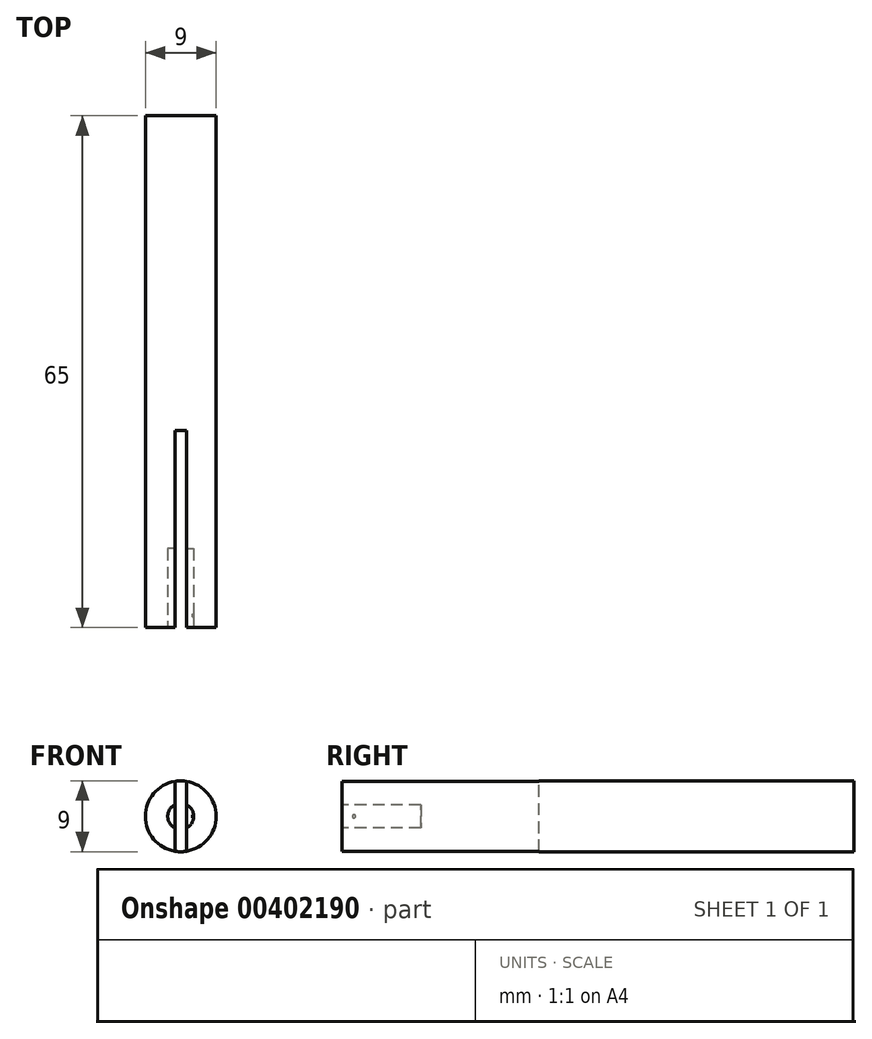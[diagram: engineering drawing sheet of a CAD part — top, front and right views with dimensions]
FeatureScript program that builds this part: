
annotation { "Feature Type Name" : "Feature", "Feature Type Description" : "" }
export const myFeature = defineFeature(function(context is Context, id is Id, definition is map)
    precondition{}
    {
        {
            var Q0;
            Q0=qCreatedBy(makeId("Front.planeOp"),FACE);
            var sketch = newSketch(context, id + "F0", { "sketchPlane" : qUnion([Q0])});
            skCircle(sketch, "E0", {"center": v(0, 0) * mm, "radius": 4.5 * mm});
            skSolve(sketch);
        }
        {
            var Q0;
            Q0=makeQuery(id+"F0.imprint","IMPRINT",FACE,{"disambiguationData":[TD([[makeQuery(id+"F0.imprint","IMPRINT",EDGE,{"derivedFrom":sQuery(id+"F0.wireOp",EDGE,"E0")}),1.0]])]});
            extrude(context, id + "F1", {"entities" : qUnion([Q0]), "oppositeDirection" : true, "depth" : 65 * mm});
        }
        {
            var Q0;
            Q0=makeQuery(id+"F1.opExtrude","CAP_FACE",FACE,{"disambiguationData":[OSD([sQuery(id+"F0.wireOp",EDGE,"E0")])],"isStart":true});
            var sketch = newSketch(context, id + "F2", { "sketchPlane" : qUnion([Q0])});
            skLineSegment(sketch, "E1.bottom", {"start": v(-0.75, -12.5) * mm, "end": v(0.75, -12.5) * mm});
            skLineSegment(sketch, "E1.top", {"start": v(-0.75, 12.5) * mm, "end": v(0.75, 12.5) * mm});
            skLineSegment(sketch, "E1.left", {"start": v(-0.75, -12.5) * mm, "end": v(-0.75, 12.5) * mm});
            skLineSegment(sketch, "E1.right", {"start": v(0.75, -12.5) * mm, "end": v(0.75, 12.5) * mm});
            skPoint(sketch, "E1.middle", {"position": v(0, 0) * mm});
            skSolve(sketch);
        }
        {
            var Q0;
            {var subQ0=sQuery(id+"F2.wireOp",EDGE,"E1.bottom");Q0=makeQuery(id+"F2.imprint","IMPRINT",FACE,{"disambiguationData":[TD([[makeQuery(id+"F2.imprint","IMPRINT",EDGE,{"derivedFrom":subQ0}),1.0]])]});}
            var Q1;
            {var subQ0=sQuery(id+"F2.wireOp",EDGE,"E1.left");var subQ1=makeQuery(id+"F1.opExtrude","CAP_EDGE",EDGE,{"disambiguationData":[OSD([sQuery(id+"F0.wireOp",EDGE,"E0")])],"isStart":true});var subQ2=makeQuery(id+"F2.imprint","INTERSECT",VERTEX,{"disambiguationData":[OD(0.0)],"derivedFrom":[subQ1,subQ0]});Q1=makeQuery(id+"F2.imprint","IMPRINT",FACE,{"disambiguationData":[TD([[makeQuery(id+"F2.imprint","IMPRINT",EDGE,{"disambiguationData":[TD([[subQ2,-1.0]])],"derivedFrom":subQ0}),-1.0]])]});}
            var Q2;
            {var subQ0=sQuery(id+"F2.wireOp",EDGE,"E1.top");Q2=makeQuery(id+"F2.imprint","IMPRINT",FACE,{"disambiguationData":[TD([[makeQuery(id+"F2.imprint","IMPRINT",EDGE,{"derivedFrom":subQ0}),-1.0]])]});}
            extrude(context, id + "F3", {"entities" : qUnion([Q0, Q1, Q2]), "operationType" : NewBodyOperationType.REMOVE, "oppositeDirection" : true, "depth" : 25 * mm});
        }
        {
            var Q0;
            {var subQ0=sQuery(id+"F0.wireOp",EDGE,"E0");Q0=makeQuery(id+"F3.boolean.opBoolean","SPLIT",FACE,{"disambiguationData":[TD([makeQuery(id+"F3.opExtrude","SWEPT_FACE",FACE,{"disambiguationData":[OSD([sQuery(id+"F2.wireOp",EDGE,"E1.right")])]})])],"derivedFrom":makeQuery(id+"F1.opExtrude","CAP_FACE",FACE,{"disambiguationData":[OSD([subQ0])],"isStart":true})});}
            var sketch = newSketch(context, id + "F4", { "sketchPlane" : qUnion([Q0])});
            skCircle(sketch, "E2", {"center": v(0, 0) * mm, "radius": 1.65 * mm});
            skSolve(sketch);
        }
        {
            var Q0;
            {var subQ0=sQuery(id+"F4.wireOp",EDGE,"E2");var subQ1=makeQuery(id+"F3.boolean.opBoolean","COPY",EDGE,{"derivedFrom":makeQuery(id+"F3.opExtrude","CAP_EDGE",EDGE,{"disambiguationData":[OSD([sQuery(id+"F2.wireOp",EDGE,"E1.right")])],"isStart":true})});var subQ2=makeQuery(id+"F4.imprint","INTERSECT",VERTEX,{"disambiguationData":[OD(0.0)],"derivedFrom":[subQ1,subQ0]});Q0=makeQuery(id+"F4.imprint","IMPRINT",FACE,{"disambiguationData":[TD([[makeQuery(id+"F4.imprint","IMPRINT",EDGE,{"disambiguationData":[TD([[subQ2,1.0]])],"derivedFrom":subQ0}),1.0]])]});}
            var Q1;
            {var subQ0=sQuery(id+"F4.wireOp",EDGE,"E2");var subQ1=makeQuery(id+"F3.boolean.opBoolean","COPY",EDGE,{"derivedFrom":makeQuery(id+"F3.opExtrude","CAP_EDGE",EDGE,{"disambiguationData":[OSD([sQuery(id+"F2.wireOp",EDGE,"E1.right")])],"isStart":true})});var subQ2=makeQuery(id+"F4.imprint","INTERSECT",VERTEX,{"disambiguationData":[OD(0.0)],"derivedFrom":[subQ1,subQ0]});Q1=makeQuery(id+"F4.imprint","IMPRINT",FACE,{"disambiguationData":[TD([[makeQuery(id+"F4.imprint","IMPRINT",EDGE,{"disambiguationData":[TD([[subQ2,-1.0]])],"derivedFrom":subQ0}),1.0]])]});}
            extrude(context, id + "F5", {"entities" : qUnion([Q0, Q1]), "operationType" : NewBodyOperationType.REMOVE, "oppositeDirection" : true, "depth" : 10 * mm});
        }
        {
            var Q0;
            Q0=qCreatedBy(makeId("Right.planeOp"),FACE);
            cPlane(context, id + "F6", {"entities" : qUnion([Q0]), "cplaneType" : CPlaneType.OFFSET, "offset" : 4.5 * mm, "width" : 150 * mm, "height" : 150 * mm});
        }
        {
            var Q0;
            Q0=qCreatedBy(id+"F6.planeOp",FACE);
            var sketch = newSketch(context, id + "F7", { "sketchPlane" : qUnion([Q0])});
            skCircle(sketch, "E3", {"center": v(1.5, 0) * mm, "radius": 0.2 * mm});
            skSolve(sketch);
        }
        {
            var Q0;
            Q0 = qSketchRegion(id + "F7", true);
            extrude(context, id + "F8", {"entities" : qUnion([Q0]), "operationType" : NewBodyOperationType.ADD, "oppositeDirection" : true, "depth" : 3 * mm});
        }
    });
